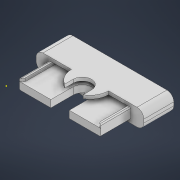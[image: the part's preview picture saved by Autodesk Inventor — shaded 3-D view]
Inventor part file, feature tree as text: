
AUTODESK INVENTOR PART (.ipt)
format: ipt  version: 2022 (Build 260153000, 153)  size: 506,368 bytes
history: native  units: mm
features: sketch x13, extrude x10, fillet x3, emboss x1
ambient origin geometry x8: Origin, YZ Plane, XZ Plane, XY Plane, X Axis, Y Axis, Z Axis, Center Point
bodies: Body1 (feature_tree)
feature tree (27):
  extrude  "Extrusion8"  Depth=10.0mm
  extrude  "Extrusion9"  Depth=13.0mm
  extrude  "Extrusion10"  Depth=10.8mm TaperAngle=0.0deg
  extrude  "Extrusion11"  Depth=17.5mm
  extrude  "Extrusion12"  Depth=2.0mm TaperAngle=0.0deg
  fillet  "Fillet5"  Radius=33.0mm
  extrude  "Extrusion13"  Depth=17.5mm
  fillet  "Fillet6"  Radius=17.5mm
  emboss  "Emboss3"
  sketch  "Sketch22"  dims[d64=0.2mm d65=0.0mm d66=0.2mm d67=0.0mm d68=1.8mm]
  extrude  "Extrusion14"  Depth=1.0mm TaperAngle=0.0deg
  extrude  "Extrusion15"  Depth=1.8mm TaperAngle=0.0deg
  fillet  "Fillet7"  Radius=1.8mm
  sketch  "Sketch25"  dims[d83=30.0mm d84=0.0mm]
  extrude  "Extrusion18"  Depth=63.0mm
  extrude  "Extrusion19"  Depth=3.8mm TaperAngle=0.0deg
  sketch  "Sketch13"  dims[d38=63.0mm d39=10.0mm]
  sketch  "Sketch15"  dims[d40=35.0mm d41=0.0mm d42=13.0mm]
  sketch  "Sketch16"  dims[d43=10.8mm d44=35.0mm d45=0.0mm]
  sketch  "Sketch17"  dims[d46=63.0mm d47=17.5mm]
  sketch  "Sketch19"  dims[d48=2.0mm d49=0.0mm d51=2.0mm d52=0.0mm d55=33.0mm d56=0.0mm]
  sketch  "Sketch20"  dims[d57=2.0mm d58=48.0mm d59=17.5mm d60=0.0mm]
  sketch  "Sketch21"  dims[d61=1.0mm d62=1.0mm d63=0.0mm]
  sketch  "Sketch23"  dims[d69=4.0mm d71=63.0mm]
  sketch  "Sketch24"  dims[d72=17.5mm d81=3.8mm d82=0.0mm]
  sketch  "Sketch28"  dims[d88=21.7mm]
  sketch  "Sketch29"
